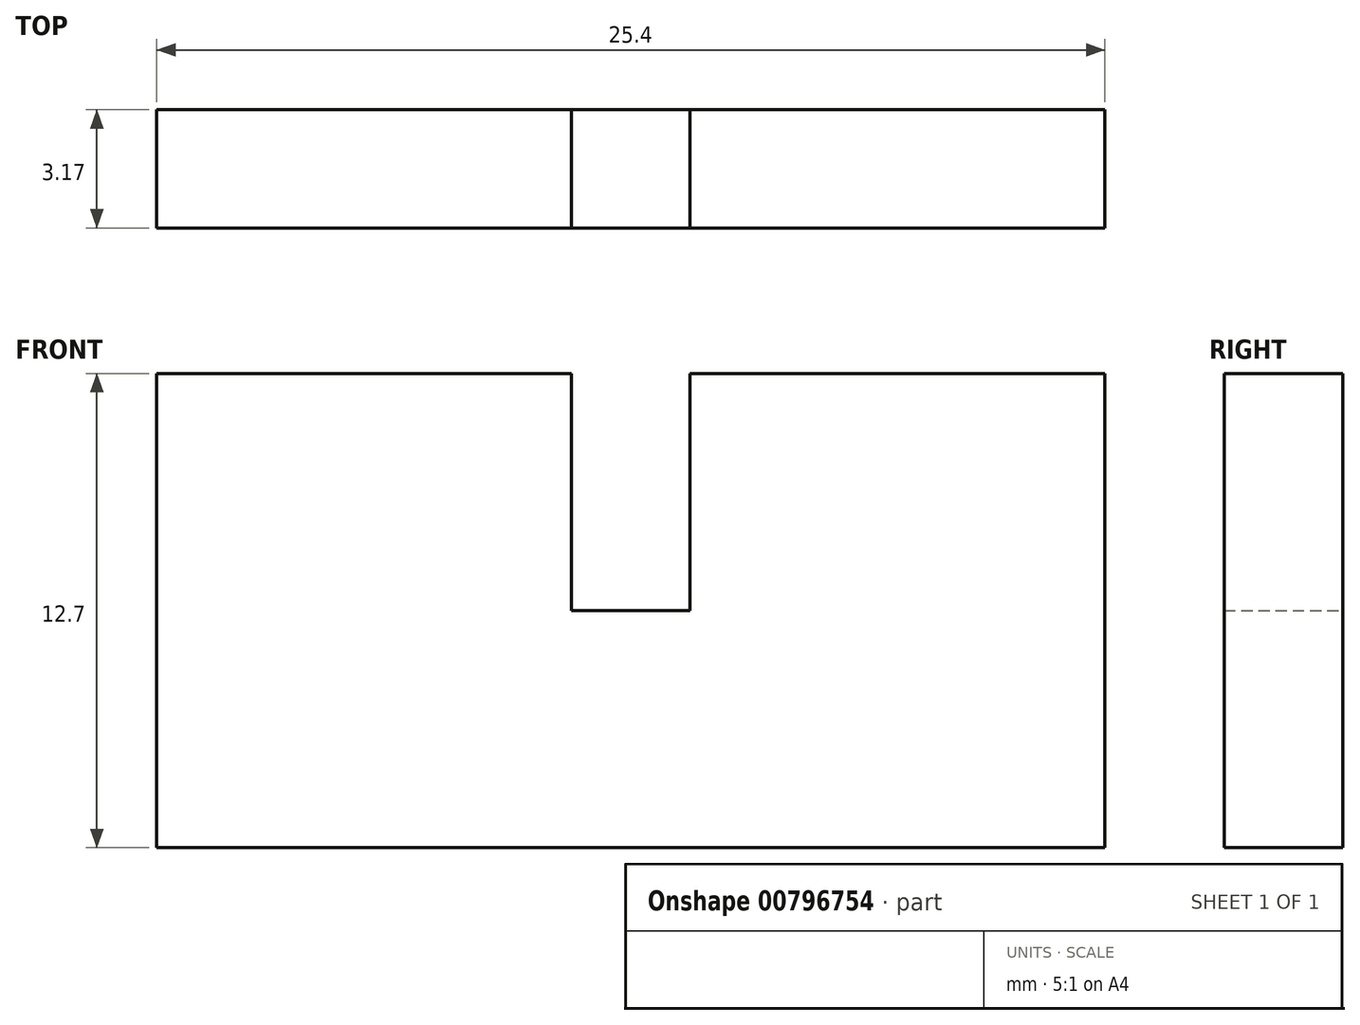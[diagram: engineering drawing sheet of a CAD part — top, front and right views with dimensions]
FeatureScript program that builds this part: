
annotation { "Feature Type Name" : "Feature", "Feature Type Description" : "" }
export const myFeature = defineFeature(function(context is Context, id is Id, definition is map)
    precondition{}
    {
        {
            var Q0;
            Q0=qCreatedBy(makeId("Front.planeOp"),FACE);
            var sketch = newSketch(context, id + "F0", { "sketchPlane" : qUnion([Q0])});
            skLineSegment(sketch, "E0.bottom", {"start": v(12.7, 6.35) * mm, "end": v(1.59, 6.35) * mm});
            skLineSegment(sketch, "E0.top", {"start": v(12.7, -6.35) * mm, "end": v(-12.7, -6.35) * mm});
            skLineSegment(sketch, "E0.left", {"start": v(12.7, 6.35) * mm, "end": v(12.7, -6.35) * mm});
            skLineSegment(sketch, "E0.right", {"start": v(-12.7, 6.35) * mm, "end": v(-12.7, -6.35) * mm});
            skPoint(sketch, "E0.middle", {"position": v(0, 0) * mm});
            skLineSegment(sketch, "E1.top", {"start": v(1.59, -6.35) * mm, "end": v(-1.59, -6.35) * mm, "construction": true});
            skLineSegment(sketch, "E1.left", {"start": v(1.59, 6.35) * mm, "end": v(1.59, -6.35) * mm, "construction": true});
            skLineSegment(sketch, "E1.right", {"start": v(-1.59, 6.35) * mm, "end": v(-1.59, -6.35) * mm, "construction": true});
            skLineSegment(sketch, "E2.top", {"start": v(-1.59, 0) * mm, "end": v(1.59, 0) * mm});
            skLineSegment(sketch, "E2.left", {"start": v(-1.59, 6.35) * mm, "end": v(-1.59, 0) * mm});
            skLineSegment(sketch, "E2.right", {"start": v(1.59, 6.35) * mm, "end": v(1.59, 0) * mm});
            skLineSegment(sketch, "E3.trimOffspring", {"start": v(-1.59, 6.35) * mm, "end": v(-12.7, 6.35) * mm});
            skSolve(sketch);
        }
        {
            var Q0;
            Q0=makeQuery(id+"F0.imprint","IMPRINT",FACE,{"disambiguationData":[TD([[makeQuery(id+"F0.imprint","IMPRINT",EDGE,{"derivedFrom":sQuery(id+"F0.wireOp",EDGE,"E0.bottom")}),1.0]])]});
            extrude(context, id + "F1", {"entities" : qUnion([Q0]), "depth" : 3.17 * mm, "offsetDistance" : 25.4 * mm});
        }
    });
